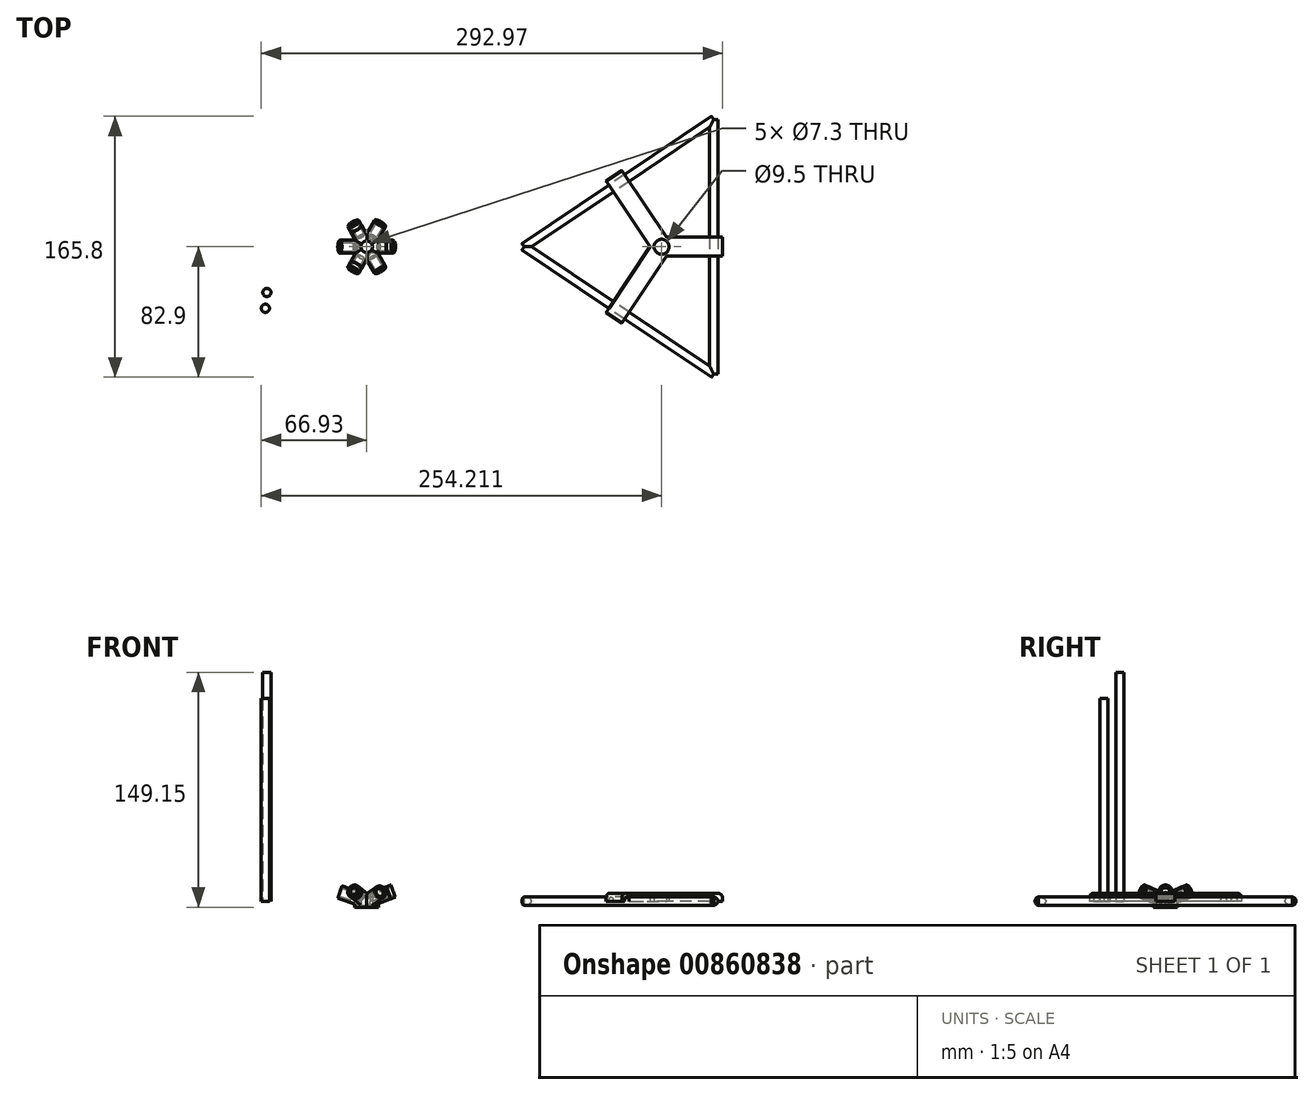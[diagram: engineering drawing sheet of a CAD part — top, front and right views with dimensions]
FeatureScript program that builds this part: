
annotation { "Feature Type Name" : "Feature", "Feature Type Description" : "" }
export const myFeature = defineFeature(function(context is Context, id is Id, definition is map)
    precondition{}
    {
        {
            assignVariable(context, id + "F0", {"name" : "espesor", "anyValue" : 1.5});
        }
        {
            assignVariable(context, id + "F1", {"name" : "longitud", "anyValue" : 18});
        }
        {
            assignVariable(context, id + "F2", {"name" : "relacion", "anyValue" : 1.11});
        }
        {
            assignVariable(context, id + "F3", {"name" : "lvarilla", "anyValue" : 145});
        }
        {
            assignVariable(context, id + "F4", {"name" : "lrecortada", "anyValue" : getVariable(context, 'lvarilla') - 2 * (getVariable(context, 'longitud') * 1.8 / 4)});
        }
        {
            assignVariable(context, id + "F5", {"name" : "lrecortadalarga", "anyValue" : (getVariable(context, 'lvarilla') * getVariable(context, 'relacion') - 2 * (getVariable(context, 'longitud') * 1.8 / 4))});
        }
        {
            var Q0;
            Q0=qCreatedBy(makeId("Front.planeOp"),FACE);
            var sketch = newSketch(context, id + "F6", { "sketchPlane" : qUnion([Q0])});
            skLineSegment(sketch, "E0", {"start": v(0, 0) * mm, "end": v(16.82, 6.42) * mm, "construction": true});
            skLineSegment(sketch, "E1", {"start": v(0, 0) * mm, "end": v(1.46, -3.83) * mm});
            skLineSegment(sketch, "E2", {"start": v(16.82, 6.42) * mm, "end": v(18.28, 2.6) * mm});
            skLineSegment(sketch, "E3", {"start": v(1.46, -3.83) * mm, "end": v(15.1, 1.38) * mm});
            skLineSegment(sketch, "E4", {"start": v(17.74, 4) * mm, "end": v(8.5, 0.46) * mm});
            skLineSegment(sketch, "E5", {"start": v(8.5, 0.46) * mm, "end": v(7.57, 2.9) * mm});
            skLineSegment(sketch, "E6", {"start": v(7.57, 2.9) * mm, "end": v(0, 0) * mm});
            skLineSegment(sketch, "E7", {"start": v(0, 0) * mm, "end": v(0, 41.35) * mm, "construction": true});
            skLineSegment(sketch, "E8", {"start": v(1.46, -3.83) * mm, "end": v(0, -3.83) * mm, "construction": true});
            skLineSegment(sketch, "E9", {"start": v(7.57, 2.9) * mm, "end": v(7.57, -3.83) * mm, "construction": true});
            skLineSegment(sketch, "E10", {"start": v(7.57, -3.83) * mm, "end": v(1.46, -3.83) * mm, "construction": true});
            skLineSegment(sketch, "E11", {"start": v(0, -3.83) * mm, "end": v(7.57, -3.83) * mm});
            skLineSegment(sketch, "E12", {"start": v(7.57, -3.83) * mm, "end": v(7.57, 2.9) * mm});
            skLineSegment(sketch, "E13", {"start": v(0, 2.9) * mm, "end": v(7.57, 2.9) * mm});
            skLineSegment(sketch, "E14", {"start": v(0, 2.9) * mm, "end": v(0, -3.83) * mm});
            skLineSegment(sketch, "E15", {"start": v(15.48, 1.52) * mm, "end": v(15.44, 1.62) * mm});
            skLineSegment(sketch, "E16", {"start": v(15.44, 1.62) * mm, "end": v(15.07, 1.47) * mm});
            skLineSegment(sketch, "E17", {"start": v(15.07, 1.47) * mm, "end": v(15.1, 1.38) * mm});
            skLineSegment(sketch, "E18.trimOffspring", {"start": v(15.48, 1.52) * mm, "end": v(18.28, 2.6) * mm});
            skSolve(sketch);
        }
        {
            var Q0;
            Q0=qCreatedBy(makeId("Front.planeOp"),FACE);
            var sketch = newSketch(context, id + "F7", { "sketchPlane" : qUnion([Q0])});
            skLineSegment(sketch, "E19", {"start": v(0, 0) * mm, "end": v(0, 45.08) * mm, "construction": true});
            skLineSegment(sketch, "E20.MirrorCS", {"start": v(-8.5, 0.13) * mm, "end": v(-7.67, 2.6) * mm});
            skLineSegment(sketch, "E21.MirrorCS", {"start": v(-17.05, 5.77) * mm, "end": v(-18.36, 1.88) * mm});
            skLineSegment(sketch, "E22.MirrorCS", {"start": v(-7.67, 2.6) * mm, "end": v(0, 0) * mm});
            skLineSegment(sketch, "E23.MirrorCS", {"start": v(0, 0) * mm, "end": v(-17.05, 5.77) * mm, "construction": true});
            skLineSegment(sketch, "E24.MirrorCS", {"start": v(0, 2.6) * mm, "end": v(-7.67, 2.6) * mm});
            skLineSegment(sketch, "E25.MirrorCS", {"start": v(-17.88, 3.3) * mm, "end": v(-8.5, 0.13) * mm});
            skLineSegment(sketch, "E26", {"start": v(-18.36, 1.88) * mm, "end": v(-1.31, -3.88) * mm});
            skLineSegment(sketch, "E27", {"start": v(0, 0) * mm, "end": v(-1.31, -3.88) * mm});
            skLineSegment(sketch, "E28", {"start": v(-1.31, -3.88) * mm, "end": v(-7.67, -3.88) * mm});
            skLineSegment(sketch, "E29", {"start": v(-1.31, -3.88) * mm, "end": v(0, -3.88) * mm});
            skLineSegment(sketch, "E30", {"start": v(0, -3.88) * mm, "end": v(0, 2.6) * mm});
            skLineSegment(sketch, "E31", {"start": v(-7.67, 2.6) * mm, "end": v(-7.67, -3.88) * mm});
            skSolve(sketch);
        }
        {
            var Q0;
            {var subQ1=sQuery(id+"F6.wireOp",EDGE,"E4");Q0=makeQuery(id+"F6.imprint","IMPRINT",FACE,{"disambiguationData":[TD([[makeQuery(id+"F6.imprint","IMPRINT",EDGE,{"derivedFrom":subQ1}),1.0]])]});}
            var Q1;
            {var subQ0=sQuery(id+"F6.wireOp",EDGE,"E1");Q1=makeQuery(id+"F6.imprint","IMPRINT",FACE,{"disambiguationData":[TD([[makeQuery(id+"F6.imprint","IMPRINT",EDGE,{"derivedFrom":subQ0}),1.0]])]});}
            var Q2;
            Q2=sQuery(id+"F6.wireOp",EDGE,"E0");
            revolve(context, id + "F8", {"surfaceOperationType" : NewSurfaceOperationType.NEW, "entities" : qUnion([Q0, Q1]), "axis" : qUnion([Q2]), "revolveType" : RevolveType.FULL});
        }
        {
            var Q0;
            {var subQ5=sQuery(id+"F7.wireOp",EDGE,"E20.MirrorCS");Q0=makeQuery(id+"F7.imprint","IMPRINT",FACE,{"disambiguationData":[TD([[makeQuery(id+"F7.imprint","IMPRINT",EDGE,{"derivedFrom":subQ5}),-1.0]])]});}
            var Q1;
            {var subQ0=sQuery(id+"F7.wireOp",EDGE,"E22.MirrorCS");Q1=makeQuery(id+"F7.imprint","IMPRINT",FACE,{"disambiguationData":[TD([[makeQuery(id+"F7.imprint","IMPRINT",EDGE,{"derivedFrom":subQ0}),-1.0]])]});}
            var Q2;
            Q2=sQuery(id+"F7.wireOp",EDGE,"E23.MirrorCS");
            revolve(context, id + "F9", {"surfaceOperationType" : NewSurfaceOperationType.NEW, "entities" : qUnion([Q0, Q1]), "axis" : qUnion([Q2]), "revolveType" : RevolveType.FULL});
        }
        {
            var Q0;
            Q0=makeQuery(id+"F8.opRevolve","SWEPT_BODY",BODY,{"disambiguationData":[OSD([sQuery(id+"F6.wireOp",EDGE,"E1"),sQuery(id+"F6.wireOp",EDGE,"E2"),sQuery(id+"F6.wireOp",EDGE,"E3"),sQuery(id+"F6.wireOp",EDGE,"E4"),sQuery(id+"F6.wireOp",EDGE,"E5"),sQuery(id+"F6.wireOp",EDGE,"E6")])]});
            var Q1;
            Q1=sQuery(id+"F6.wireOp",EDGE,"E7");
            circularPattern(context, id + "F10", {"operationType" : NewBodyOperationType.ADD, "entities" : qUnion([Q0]), "axis" : qUnion([Q1]), "angle" : 360 * degree, "instanceCount" : 3, "equalSpace" : true});
        }
        {
            var Q0;
            Q0=makeQuery(id+"FgpRCOrkwi8NXZ9_2.boolean.opBoolean","SPLIT",BODY,{"disambiguationData":[OD(1.0)],"derivedFrom":makeQuery(id+"F9.opRevolve","SWEPT_BODY",BODY,{"disambiguationData":[OSD([sQuery(id+"F7.wireOp",EDGE,"E20.MirrorCS"),sQuery(id+"F7.wireOp",EDGE,"E21.MirrorCS"),sQuery(id+"F7.wireOp",EDGE,"E22.MirrorCS"),sQuery(id+"F7.wireOp",EDGE,"E25.MirrorCS"),sQuery(id+"F7.wireOp",EDGE,"E26"),sQuery(id+"F7.wireOp",EDGE,"E27")])]})});
            var Q1;
            Q1=sQuery(id+"F7.wireOp",EDGE,"E19");
            circularPattern(context, id + "F11", {"entities" : qUnion([Q0]), "axis" : qUnion([Q1]), "angle" : 360 * degree, "instanceCount" : 3, "equalSpace" : true});
        }
        {
            var Q0;
            {var subQ0=sQuery(id+"F6.wireOp",EDGE,"E1");Q0=makeQuery(id+"F6.imprint","IMPRINT",FACE,{"disambiguationData":[TD([[makeQuery(id+"F6.imprint","IMPRINT",EDGE,{"derivedFrom":subQ0}),-1.0]])]});}
            var Q1;
            {var subQ0=sQuery(id+"F6.wireOp",EDGE,"E1");Q1=makeQuery(id+"F6.imprint","IMPRINT",FACE,{"disambiguationData":[TD([[makeQuery(id+"F6.imprint","IMPRINT",EDGE,{"derivedFrom":subQ0}),1.0]])]});}
            var Q2;
            {var subQ0=sQuery(id+"F6.wireOp",EDGE,"E11");var subQ3=sQuery(id+"F6.wireOp",EDGE,"E12");var subQ5=makeQuery(id+"F6.imprint","INTERSECT",VERTEX,{"derivedFrom":[subQ0,subQ3]});Q2=makeQuery(id+"F6.imprint","IMPRINT",FACE,{"disambiguationData":[TD([[makeQuery(id+"F6.imprint","IMPRINT",EDGE,{"disambiguationData":[TD([[subQ5,-1.0]])],"derivedFrom":subQ3}),1.0]])]});}
            var Q3;
            {var subQ0=sQuery(id+"F6.wireOp",EDGE,"E6");Q3=makeQuery(id+"F6.imprint","IMPRINT",FACE,{"disambiguationData":[TD([[makeQuery(id+"F6.imprint","IMPRINT",EDGE,{"derivedFrom":subQ0}),-1.0]])]});}
            var Q4;
            Q4=sQuery(id+"F6.wireOp",EDGE,"E13");
            var Q5;
            Q5=sQuery(id+"F6.wireOp",EDGE,"E14");
            var Q6;
            Q6=sQuery(id+"F6.wireOp",EDGE,"E7");
            revolve(context, id + "F12", {"surfaceOperationType" : NewSurfaceOperationType.NEW, "entities" : qUnion([Q0, Q1, Q2, Q3]), "surfaceEntities" : qUnion([Q4, Q5]), "axis" : qUnion([Q6]), "revolveType" : RevolveType.FULL});
        }
        {
            var Q0;
            {var subQ0=sQuery(id+"F7.wireOp",EDGE,"E22.MirrorCS");Q0=makeQuery(id+"F7.imprint","IMPRINT",FACE,{"disambiguationData":[TD([[makeQuery(id+"F7.imprint","IMPRINT",EDGE,{"derivedFrom":subQ0}),1.0]])]});}
            var Q1;
            {var subQ0=sQuery(id+"F7.wireOp",EDGE,"E22.MirrorCS");Q1=makeQuery(id+"F7.imprint","IMPRINT",FACE,{"disambiguationData":[TD([[makeQuery(id+"F7.imprint","IMPRINT",EDGE,{"derivedFrom":subQ0}),-1.0]])]});}
            var Q2;
            {var subQ0=sQuery(id+"F7.wireOp",EDGE,"E27");Q2=makeQuery(id+"F7.imprint","IMPRINT",FACE,{"disambiguationData":[TD([[makeQuery(id+"F7.imprint","IMPRINT",EDGE,{"derivedFrom":subQ0}),1.0]])]});}
            var Q3;
            {var subQ0=sQuery(id+"F7.wireOp",EDGE,"E28");Q3=makeQuery(id+"F7.imprint","IMPRINT",FACE,{"disambiguationData":[TD([[makeQuery(id+"F7.imprint","IMPRINT",EDGE,{"derivedFrom":subQ0}),-1.0]])]});}
            var Q4;
            Q4=sQuery(id+"F7.wireOp",EDGE,"E19");
            revolve(context, id + "F13", {"surfaceOperationType" : NewSurfaceOperationType.NEW, "entities" : qUnion([Q0, Q1, Q2, Q3]), "axis" : qUnion([Q4]), "revolveType" : RevolveType.FULL});
        }
        {
            var Q0;
            Q0=makeQuery(id+"F10.opPattern","COPY",EDGE,{"derivedFrom":makeQuery(id+"F8.opRevolve","SWEPT_EDGE",EDGE,{"disambiguationData":[OSD([sQuery(id+"F6.wireOp",EDGE,"E2"),sQuery(id+"F6.wireOp",EDGE,"E4")])]}),"instanceName":"5"});
            var Q1;
            Q1=makeQuery(id+"F10.opPattern","COPY",EDGE,{"derivedFrom":makeQuery(id+"F8.opRevolve","SWEPT_EDGE",EDGE,{"disambiguationData":[OSD([sQuery(id+"F6.wireOp",EDGE,"E2"),sQuery(id+"F6.wireOp",EDGE,"E4")])]}),"instanceName":"4"});
            var Q2;
            Q2=makeQuery(id+"F8.opRevolve","SWEPT_EDGE",EDGE,{"disambiguationData":[OSD([sQuery(id+"F6.wireOp",EDGE,"E2"),sQuery(id+"F6.wireOp",EDGE,"E4")])]});
            var Q3;
            Q3=makeQuery(id+"F10.opPattern","COPY",EDGE,{"derivedFrom":makeQuery(id+"F8.opRevolve","SWEPT_EDGE",EDGE,{"disambiguationData":[OSD([sQuery(id+"F6.wireOp",EDGE,"E2"),sQuery(id+"F6.wireOp",EDGE,"E4")])]}),"instanceName":"1"});
            var Q4;
            Q4=makeQuery(id+"F10.opPattern","COPY",EDGE,{"derivedFrom":makeQuery(id+"F8.opRevolve","SWEPT_EDGE",EDGE,{"disambiguationData":[OSD([sQuery(id+"F6.wireOp",EDGE,"E2"),sQuery(id+"F6.wireOp",EDGE,"E4")])]}),"instanceName":"2"});
            var Q5;
            Q5=makeQuery(id+"F10.opPattern","COPY",EDGE,{"derivedFrom":makeQuery(id+"F8.opRevolve","SWEPT_EDGE",EDGE,{"disambiguationData":[OSD([sQuery(id+"F6.wireOp",EDGE,"E2"),sQuery(id+"F6.wireOp",EDGE,"E4")])]}),"instanceName":"3"});
            var Q6;
            Q6=makeQuery(id+"F11.opPattern","COPY",EDGE,{"derivedFrom":makeQuery(id+"F9.opRevolve","SWEPT_EDGE",EDGE,{"disambiguationData":[OSD([sQuery(id+"F7.wireOp",EDGE,"E21.MirrorCS"),sQuery(id+"F7.wireOp",EDGE,"E25.MirrorCS")])]}),"instanceName":"2"});
            var Q7;
            Q7=makeQuery(id+"F9.opRevolve","SWEPT_EDGE",EDGE,{"disambiguationData":[OSD([sQuery(id+"F7.wireOp",EDGE,"E21.MirrorCS"),sQuery(id+"F7.wireOp",EDGE,"E25.MirrorCS")])]});
            var Q8;
            Q8=makeQuery(id+"F11.opPattern","COPY",EDGE,{"derivedFrom":makeQuery(id+"F9.opRevolve","SWEPT_EDGE",EDGE,{"disambiguationData":[OSD([sQuery(id+"F7.wireOp",EDGE,"E21.MirrorCS"),sQuery(id+"F7.wireOp",EDGE,"E25.MirrorCS")])]}),"instanceName":"1"});
            chamfer(context, id + "F14", {"entities" : qUnion([Q0, Q1, Q2, Q3, Q4, Q5, Q6, Q7, Q8]), "width" : (getVariable(context, 'espesor') / 2) * mm, "tangentPropagation" : true});
        }
        {
            var Q0;
            Q0=qCreatedBy(makeId("Top.planeOp"),FACE);
            var sketch = newSketch(context, id + "F15", { "sketchPlane" : qUnion([Q0])});
            skCircle(sketch, "E32", {"center": v(-64.33, -39.09) * mm, "radius": 2.6 * mm});
            skCircle(sketch, "E33", {"center": v(-63.38, -29.03) * mm, "radius": 2.6 * mm});
            skSolve(sketch);
        }
        {
            var Q0;
            Q0=makeQuery(id+"F15.imprint","IMPRINT",FACE,{"disambiguationData":[TD([[makeQuery(id+"F15.imprint","IMPRINT",EDGE,{"derivedFrom":sQuery(id+"F15.wireOp",EDGE,"E32")}),1.0]])]});
            extrude(context, id + "F16", {"entities" : qUnion([Q0]), "depth" : (getVariable(context, 'lrecortada')) * mm, "offsetDistance" : 25 * mm});
        }
        {
            var Q0;
            Q0=makeQuery(id+"F15.imprint","IMPRINT",FACE,{"disambiguationData":[TD([[makeQuery(id+"F15.imprint","IMPRINT",EDGE,{"derivedFrom":sQuery(id+"F15.wireOp",EDGE,"E33")}),1.0]])]});
            extrude(context, id + "F17", {"entities" : qUnion([Q0]), "depth" : (getVariable(context, 'lrecortadalarga')) * mm, "offsetDistance" : 25 * mm});
        }
        {
            var Q0;
            Q0=qCreatedBy(makeId("Top.planeOp"),FACE);
            var sketch = newSketch(context, id + "F18", { "sketchPlane" : qUnion([Q0])});
            skCircle(sketch, "E34", {"center": v(0, 0) * mm, "radius": 3.65 * mm});
            skSolve(sketch);
        }
        {
            var Q0;
            Q0=qSketchRegion(id+"F18",true);
            extrude(context, id + "F19", {"entities" : qUnion([Q0]), "operationType" : NewBodyOperationType.REMOVE, "depth" : 200 * mm, "offsetDistance" : 25 * mm, "symmetric" : true});
        }
        {
            var Q0;
            Q0=qCreatedBy(makeId("Top.planeOp"),FACE);
            var sketch = newSketch(context, id + "F20", { "sketchPlane" : qUnion([Q0])});
            skLineSegment(sketch, "E35", {"start": v(100, 0) * mm, "end": v(220.44, 80.74) * mm});
            skLineSegment(sketch, "E36", {"start": v(100, 0) * mm, "end": v(220.44, -80.74) * mm});
            skLineSegment(sketch, "E37", {"start": v(220.44, -80.74) * mm, "end": v(220.44, 80.74) * mm});
            skLineSegment(sketch, "E38", {"start": v(100, 0) * mm, "end": v(1382.5, 0) * mm, "construction": true});
            skLineSegment(sketch, "E39.0", {"start": v(98.55, 2.16) * mm, "end": v(219, 82.9) * mm});
            skLineSegment(sketch, "E40.0", {"start": v(223.04, -80.74) * mm, "end": v(223.04, 80.74) * mm});
            skLineSegment(sketch, "E41.0", {"start": v(98.55, -2.16) * mm, "end": v(219, -82.9) * mm});
            skLineSegment(sketch, "E42", {"start": v(98.55, 2.16) * mm, "end": v(100, 0) * mm});
            skLineSegment(sketch, "E43", {"start": v(98.55, -2.16) * mm, "end": v(100, 0) * mm});
            skLineSegment(sketch, "E44", {"start": v(220.44, 80.74) * mm, "end": v(219, 82.9) * mm});
            skLineSegment(sketch, "E45", {"start": v(220.44, 80.74) * mm, "end": v(223.04, 80.74) * mm});
            skLineSegment(sketch, "E46", {"start": v(223.04, -80.74) * mm, "end": v(220.44, -80.74) * mm});
            skLineSegment(sketch, "E47", {"start": v(220.44, -80.74) * mm, "end": v(219, -82.9) * mm});
            skLineSegment(sketch, "E48", {"start": v(160.22, 40.37) * mm, "end": v(183.92, 5.02) * mm, "construction": true});
            skLineSegment(sketch, "E49", {"start": v(160.22, -40.37) * mm, "end": v(183.1, -6.24) * mm, "construction": true});
            skLineSegment(sketch, "E50", {"start": v(162.09, 48.36) * mm, "end": v(190.48, 6) * mm});
            skLineSegment(sketch, "E51", {"start": v(190.48, -6) * mm, "end": v(162.09, -48.36) * mm});
            skLineSegment(sketch, "E52", {"start": v(152.12, 41.68) * mm, "end": v(180.06, 0) * mm});
            skLineSegment(sketch, "E53", {"start": v(180.06, 0) * mm, "end": v(152.12, -41.68) * mm});
            skLineSegment(sketch, "E54", {"start": v(226.04, 6) * mm, "end": v(190.48, 6) * mm});
            skLineSegment(sketch, "E55.MirrorCS", {"start": v(226.04, -6) * mm, "end": v(190.48, -6) * mm});
            skPoint(sketch, "E56.orphan", {"position": v(194.5, 0) * mm});
            skLineSegment(sketch, "E57", {"start": v(226.04, 6) * mm, "end": v(226.04, -6) * mm});
            skLineSegment(sketch, "E58", {"start": v(152.12, -41.68) * mm, "end": v(162.09, -48.36) * mm});
            skLineSegment(sketch, "E59", {"start": v(162.09, 48.36) * mm, "end": v(152.12, 41.68) * mm});
            skCircle(sketch, "E60", {"center": v(187.28, 0) * mm, "radius": 4.75 * mm});
            skSolve(sketch);
        }
        {
            var Q0;
            Q0=makeQuery(id+"F20.imprint","IMPRINT",FACE,{"disambiguationData":[TD([[makeQuery(id+"F20.imprint","IMPRINT",EDGE,{"derivedFrom":sQuery(id+"F20.wireOp",EDGE,"E35")}),1.0]])]});
            var Q1;
            Q1=sQuery(id+"F20.wireOp",EDGE,"E35");
            revolve(context, id + "F21", {"surfaceOperationType" : NewSurfaceOperationType.NEW, "entities" : qUnion([Q0]), "axis" : qUnion([Q1]), "revolveType" : RevolveType.FULL});
        }
        {
            var Q0;
            Q0=makeQuery(id+"F20.imprint","IMPRINT",FACE,{"disambiguationData":[TD([[makeQuery(id+"F20.imprint","IMPRINT",EDGE,{"derivedFrom":sQuery(id+"F20.wireOp",EDGE,"E36")}),-1.0]])]});
            var Q1;
            Q1=sQuery(id+"F20.wireOp",EDGE,"E36");
            revolve(context, id + "F22", {"operationType" : NewBodyOperationType.ADD, "surfaceOperationType" : NewSurfaceOperationType.NEW, "entities" : qUnion([Q0]), "axis" : qUnion([Q1]), "revolveType" : RevolveType.FULL});
        }
        {
            var Q0;
            Q0=makeQuery(id+"F20.imprint","IMPRINT",FACE,{"disambiguationData":[TD([[makeQuery(id+"F20.imprint","IMPRINT",EDGE,{"derivedFrom":sQuery(id+"F20.wireOp",EDGE,"E37")}),-1.0]])]});
            var Q1;
            Q1=sQuery(id+"F20.wireOp",EDGE,"E37");
            revolve(context, id + "F23", {"operationType" : NewBodyOperationType.ADD, "surfaceOperationType" : NewSurfaceOperationType.NEW, "entities" : qUnion([Q0]), "axis" : qUnion([Q1]), "revolveType" : RevolveType.FULL});
        }
        {
            var Q0;
            {var subQ12=sQuery(id+"F20.wireOp",EDGE,"E35");var subQ14=sQuery(id+"F20.wireOp",EDGE,"E52");var subQ15=makeQuery(id+"F20.imprint","INTERSECT",VERTEX,{"derivedFrom":[subQ12,subQ14]});Q0=makeQuery(id+"F20.imprint","IMPRINT",FACE,{"disambiguationData":[TD([[makeQuery(id+"F20.imprint","IMPRINT",EDGE,{"disambiguationData":[TD([[subQ15,-1.0]])],"derivedFrom":subQ12}),-1.0]])]});}
            var Q1;
            {var subQ5=sQuery(id+"F20.wireOp",EDGE,"E58");Q1=makeQuery(id+"F20.imprint","IMPRINT",FACE,{"disambiguationData":[TD([[makeQuery(id+"F20.imprint","IMPRINT",EDGE,{"derivedFrom":subQ5}),1.0]])]});}
            var Q2;
            {var subQ5=sQuery(id+"F20.wireOp",EDGE,"E57");Q2=makeQuery(id+"F20.imprint","IMPRINT",FACE,{"disambiguationData":[TD([[makeQuery(id+"F20.imprint","IMPRINT",EDGE,{"derivedFrom":subQ5}),-1.0]])]});}
            var Q3;
            {var subQ5=sQuery(id+"F20.wireOp",EDGE,"E59");Q3=makeQuery(id+"F20.imprint","IMPRINT",FACE,{"disambiguationData":[TD([[makeQuery(id+"F20.imprint","IMPRINT",EDGE,{"derivedFrom":subQ5}),1.0]])]});}
            var Q4;
            {var subQ0=sQuery(id+"F20.wireOp",EDGE,"E53");var subQ1=sQuery(id+"F20.wireOp",EDGE,"E36");var subQ2=makeQuery(id+"F20.imprint","INTERSECT",VERTEX,{"derivedFrom":[subQ1,subQ0]});Q4=makeQuery(id+"F20.imprint","IMPRINT",FACE,{"disambiguationData":[TD([[makeQuery(id+"F20.imprint","IMPRINT",EDGE,{"disambiguationData":[TD([[subQ2,-1.0]])],"derivedFrom":subQ1}),-1.0]])]});}
            var Q5;
            {var subQ0=sQuery(id+"F20.wireOp",EDGE,"E55.MirrorCS");var subQ1=sQuery(id+"F20.wireOp",EDGE,"E37");var subQ2=makeQuery(id+"F20.imprint","INTERSECT",VERTEX,{"derivedFrom":[subQ1,subQ0]});Q5=makeQuery(id+"F20.imprint","IMPRINT",FACE,{"disambiguationData":[TD([[makeQuery(id+"F20.imprint","IMPRINT",EDGE,{"disambiguationData":[TD([[subQ2,-1.0]])],"derivedFrom":subQ1}),-1.0]])]});}
            var Q6;
            {var subQ0=sQuery(id+"F20.wireOp",EDGE,"E52");var subQ1=sQuery(id+"F20.wireOp",EDGE,"E35");var subQ2=makeQuery(id+"F20.imprint","INTERSECT",VERTEX,{"derivedFrom":[subQ1,subQ0]});Q6=makeQuery(id+"F20.imprint","IMPRINT",FACE,{"disambiguationData":[TD([[makeQuery(id+"F20.imprint","IMPRINT",EDGE,{"disambiguationData":[TD([[subQ2,-1.0]])],"derivedFrom":subQ1}),1.0]])]});}
            var Q7;
            Q7=makeQuery(id+"F20.imprint","IMPRINT",FACE,{"disambiguationData":[TD([[makeQuery(id+"F20.imprint","IMPRINT",EDGE,{"derivedFrom":sQuery(id+"F20.wireOp",EDGE,"E60")}),-1.0]])]});
            extrude(context, id + "F24", {"entities" : qUnion([Q0, Q1, Q2, Q3, Q4, Q5, Q6, Q7]), "depth" : 5 * mm, "offsetDistance" : 25 * mm});
        }
        {
            var Q0;
            Q0=makeQuery(id+"F24.opExtrude","CAP_EDGE",EDGE,{"disambiguationData":[OSD([sQuery(id+"F20.wireOp",EDGE,"E58")])],"isStart":false});
            var Q1;
            Q1=makeQuery(id+"F24.opExtrude","CAP_EDGE",EDGE,{"disambiguationData":[OSD([sQuery(id+"F20.wireOp",EDGE,"E57")])],"isStart":false});
            var Q2;
            Q2=makeQuery(id+"F24.opExtrude","CAP_EDGE",EDGE,{"disambiguationData":[OSD([sQuery(id+"F20.wireOp",EDGE,"E59")])],"isStart":false});
            fillet(context, id + "F25", {"entities" : qUnion([Q0, Q1, Q2]), "radius" : 3 * mm, "tangentPropagation" : true, "allowEdgeOverflow" : false});
        }
        {
            var Q0;
            Q0=makeQuery(id+"F21.opRevolve","SWEPT_BODY",BODY,{"disambiguationData":[OSD([sQuery(id+"F20.wireOp",EDGE,"E35"),sQuery(id+"F20.wireOp",EDGE,"E39.0"),sQuery(id+"F20.wireOp",EDGE,"E42"),sQuery(id+"F20.wireOp",EDGE,"E44")])]});
            var Q1;
            Q1=makeQuery(id+"F24.opExtrude","SWEPT_BODY",BODY,{"disambiguationData":[OSD([sQuery(id+"F20.wireOp",EDGE,"E50"),sQuery(id+"F20.wireOp",EDGE,"E51"),sQuery(id+"F20.wireOp",EDGE,"E52"),sQuery(id+"F20.wireOp",EDGE,"E53"),sQuery(id+"F20.wireOp",EDGE,"E54"),sQuery(id+"F20.wireOp",EDGE,"E55.MirrorCS"),sQuery(id+"F20.wireOp",EDGE,"E57"),sQuery(id+"F20.wireOp",EDGE,"E58"),sQuery(id+"F20.wireOp",EDGE,"E59"),sQuery(id+"F20.wireOp",EDGE,"E60")])]});
            booleanBodies(context, id + "F26", {"operationType" : BooleanOperationType.SUBTRACTION, "tools" : qUnion([Q0]), "targets" : qUnion([Q1]), "keepTools" : true});
        }
    });
